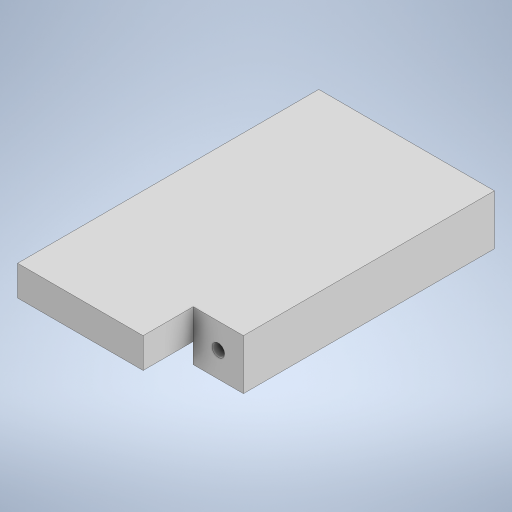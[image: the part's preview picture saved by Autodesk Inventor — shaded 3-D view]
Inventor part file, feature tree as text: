
AUTODESK INVENTOR PART (.ipt)
format: ipt  version: 2023 (Build 270158000, 158)  size: 226,816 bytes
history: native  units: in
note: dims shown in document units (in); Inventor stores cm internally (conversion verified against a paired STEP export)
features: extrude x3, sketch x3
ambient origin geometry x8: Origin, YZ Plane, XZ Plane, XY Plane, X Axis, Y Axis, Z Axis, Center Point
bodies: Body1 (feature_tree)
feature tree (6):
  extrude  "Extrusion2"  Depth=0.7874in
  extrude  "Extrusion5"  Depth=0.3937in
  extrude  "Extrusion7"  Depth=0.9843in TaperAngle=0.0deg
  sketch  "Sketch1"  dims[d0=0.7874in d1=0.7874in]
  sketch  "Sketch5"  dims[d5=0.3937in d6=0.3937in]
  sketch  "Sketch7"  dims[d7=0.1969in d8=0.9843in d9=0.0in d17=0.3543in d18=2.9528in d19=0.0in d25=1.9685in d26=0.4724in d27=4.7244in d28=0.0in]
